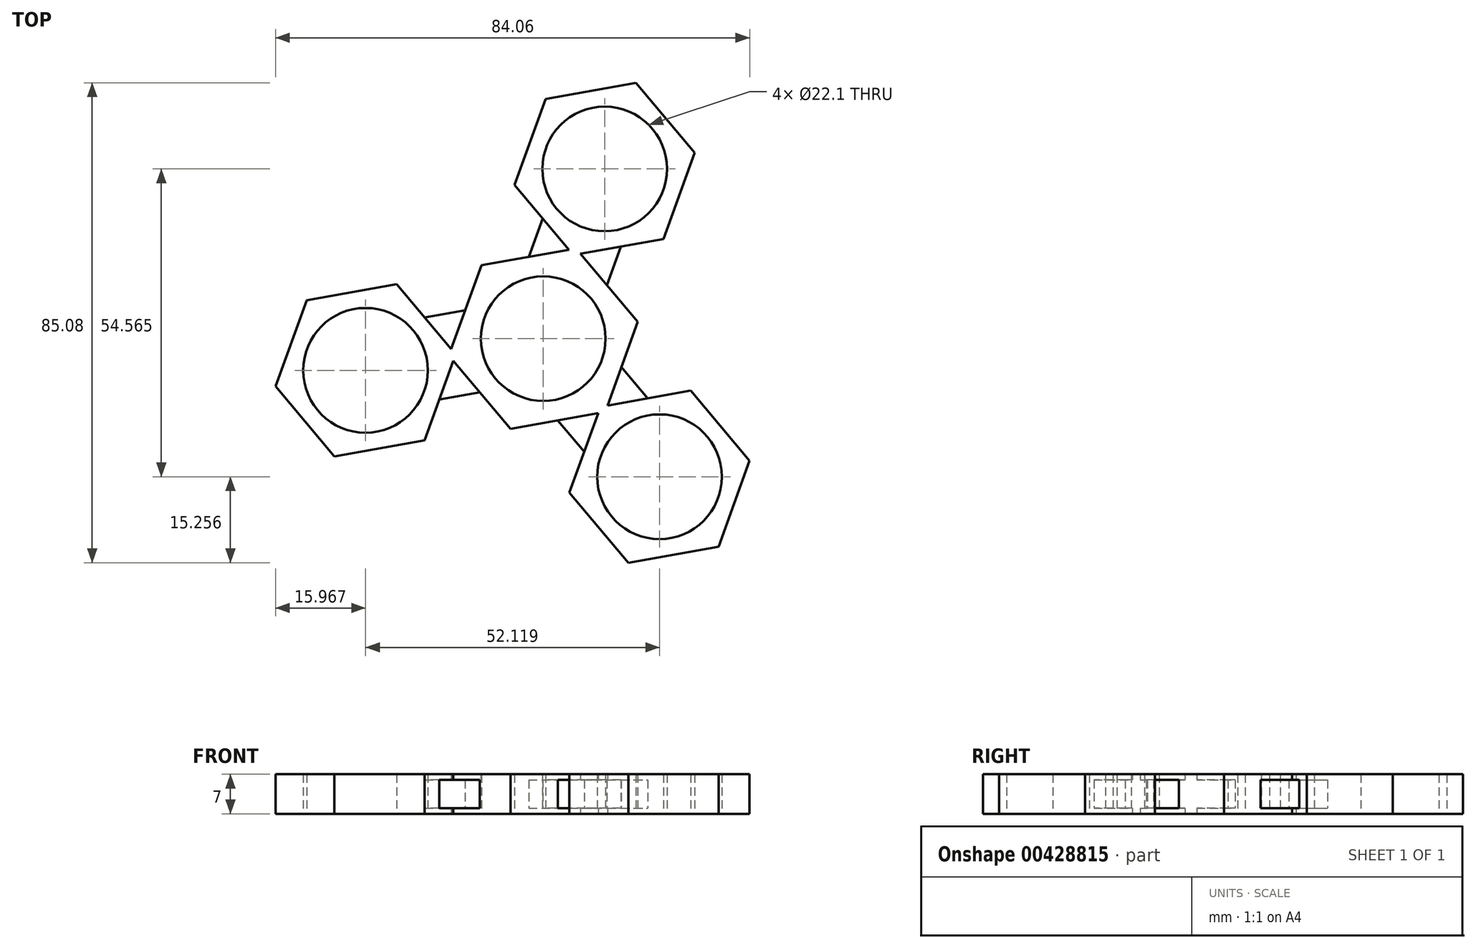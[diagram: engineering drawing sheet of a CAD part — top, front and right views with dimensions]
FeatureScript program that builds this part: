
annotation { "Feature Type Name" : "Feature", "Feature Type Description" : "" }
export const myFeature = defineFeature(function(context is Context, id is Id, definition is map)
    precondition{}
    {
        {
            var Q0;
            Q0=qCreatedBy(makeId("Top.planeOp"),FACE);
            var sketch = newSketch(context, id + "F0", { "sketchPlane" : qUnion([Q0])});
            skCircle(sketch, "E0", {"center": v(0, 0) * mm, "radius": 11.05 * mm});
            skCircle(sketch, "E1.cCircle", {"center": v(0, 0) * mm, "radius": 14.73 * mm, "construction": true});
            skLineSegment(sketch, "E1.0", {"start": v(16.75, 2.99) * mm, "end": v(10.96, -13.01) * mm});
            skLineSegment(sketch, "E1.1", {"start": v(10.96, -13.01) * mm, "end": v(-5.79, -16) * mm});
            skLineSegment(sketch, "E1.2", {"start": v(-5.79, -16) * mm, "end": v(-16.75, -2.99) * mm});
            skLineSegment(sketch, "E1.3", {"start": v(-16.75, -2.99) * mm, "end": v(-10.96, 13.01) * mm});
            skLineSegment(sketch, "E1.4", {"start": v(-10.96, 13.01) * mm, "end": v(5.79, 16) * mm});
            skLineSegment(sketch, "E1.5", {"start": v(5.79, 16) * mm, "end": v(16.75, 2.99) * mm});
            skPoint(sketch, "E1.0.midPoint", {"position": v(13.85, -5.01) * mm});
            skLineSegment(sketch, "E2", {"start": v(0, 0) * mm, "end": v(10.89, 30.1) * mm});
            skCircle(sketch, "E3", {"center": v(10.89, 30.1) * mm, "radius": 11.05 * mm});
            skCircle(sketch, "E4.0", {"center": v(10.89, 30.1) * mm, "radius": 14.05 * mm});
            skCircle(sketch, "E5.cCircle", {"center": v(10.89, 30.1) * mm, "radius": 14.05 * mm, "construction": true});
            skLineSegment(sketch, "E5.0", {"start": v(-5.08, 27.24) * mm, "end": v(0.44, 42.5) * mm});
            skLineSegment(sketch, "E5.1", {"start": v(0.44, 42.5) * mm, "end": v(16.4, 45.35) * mm});
            skLineSegment(sketch, "E5.2", {"start": v(16.4, 45.35) * mm, "end": v(26.86, 32.94) * mm});
            skLineSegment(sketch, "E5.3", {"start": v(26.86, 32.94) * mm, "end": v(21.34, 17.68) * mm});
            skLineSegment(sketch, "E5.4", {"start": v(21.34, 17.68) * mm, "end": v(5.37, 14.84) * mm});
            skLineSegment(sketch, "E5.5", {"start": v(5.37, 14.84) * mm, "end": v(-5.08, 27.24) * mm});
            skPoint(sketch, "E5.0.midPoint", {"position": v(-2.32, 34.87) * mm});
            skLineSegment(sketch, "E6", {"start": v(-2.59, 14.5) * mm, "end": v(0, 21.65) * mm});
            skLineSegment(sketch, "E7.MirrorCS", {"start": v(11.27, 9.5) * mm, "end": v(13.85, 16.64) * mm});
            skCircle(sketch, "E8.1.0", {"center": v(-31.5, -5.62) * mm, "radius": 14.05 * mm, "construction": true});
            skLineSegment(sketch, "E8.1.1", {"start": v(-11.27, -9.5) * mm, "end": v(-18.75, -10.83) * mm});
            skLineSegment(sketch, "E8.1.2", {"start": v(-15.53, -2.77) * mm, "end": v(-21.05, -18.02) * mm});
            skLineSegment(sketch, "E8.1.3", {"start": v(-25.98, 9.64) * mm, "end": v(-15.53, -2.77) * mm});
            skLineSegment(sketch, "E8.1.4", {"start": v(-13.85, 5.01) * mm, "end": v(-21.34, 3.68) * mm});
            skLineSegment(sketch, "E8.1.5", {"start": v(-41.96, 6.8) * mm, "end": v(-25.98, 9.64) * mm});
            skLineSegment(sketch, "E8.1.6", {"start": v(-47.47, -8.46) * mm, "end": v(-41.96, 6.8) * mm});
            skLineSegment(sketch, "E8.1.7", {"start": v(-37.02, -20.87) * mm, "end": v(-47.47, -8.46) * mm});
            skLineSegment(sketch, "E8.1.8", {"start": v(-21.05, -18.02) * mm, "end": v(-37.02, -20.87) * mm});
            skCircle(sketch, "E8.1.9", {"center": v(-31.5, -5.62) * mm, "radius": 11.05 * mm});
            skCircle(sketch, "E8.2.0", {"center": v(20.62, -24.47) * mm, "radius": 14.05 * mm, "construction": true});
            skLineSegment(sketch, "E8.2.1", {"start": v(13.85, -5.01) * mm, "end": v(18.75, -10.83) * mm});
            skLineSegment(sketch, "E8.2.2", {"start": v(10.16, -12.07) * mm, "end": v(26.14, -9.22) * mm});
            skLineSegment(sketch, "E8.2.3", {"start": v(4.64, -27.32) * mm, "end": v(10.16, -12.07) * mm});
            skLineSegment(sketch, "E8.2.4", {"start": v(2.59, -14.5) * mm, "end": v(7.48, -20.32) * mm});
            skLineSegment(sketch, "E8.2.5", {"start": v(15.1, -39.73) * mm, "end": v(4.64, -27.32) * mm});
            skLineSegment(sketch, "E8.2.6", {"start": v(31.07, -36.88) * mm, "end": v(15.1, -39.73) * mm});
            skLineSegment(sketch, "E8.2.7", {"start": v(36.59, -21.63) * mm, "end": v(31.07, -36.88) * mm});
            skLineSegment(sketch, "E8.2.8", {"start": v(26.14, -9.22) * mm, "end": v(36.59, -21.63) * mm});
            skCircle(sketch, "E8.2.9", {"center": v(20.62, -24.47) * mm, "radius": 11.05 * mm});
            skSolve(sketch);
        }
        {
            var Q0;
            {var subQ0=sQuery(id+"F0.wireOp",EDGE,"E5.1");var subQ1=sQuery(id+"F0.wireOp",EDGE,"E4.0");var subQ2=makeQuery(id+"F0.imprint","INTERSECT",VERTEX,{"derivedFrom":[subQ1,subQ0]});Q0=makeQuery(id+"F0.imprint","IMPRINT",FACE,{"disambiguationData":[TD([[makeQuery(id+"F0.imprint","IMPRINT",EDGE,{"disambiguationData":[TD([[subQ2,1.0]])],"derivedFrom":subQ1}),-1.0]])]});}
            var Q1;
            {var subQ0=sQuery(id+"F0.wireOp",EDGE,"E5.1");var subQ1=sQuery(id+"F0.wireOp",EDGE,"E4.0");var subQ2=makeQuery(id+"F0.imprint","INTERSECT",VERTEX,{"derivedFrom":[subQ1,subQ0]});Q1=makeQuery(id+"F0.imprint","IMPRINT",FACE,{"disambiguationData":[TD([[makeQuery(id+"F0.imprint","IMPRINT",EDGE,{"disambiguationData":[TD([[subQ2,-1.0]])],"derivedFrom":subQ1}),-1.0]])]});}
            var Q2;
            {var subQ0=sQuery(id+"F0.wireOp",EDGE,"E5.2");var subQ1=sQuery(id+"F0.wireOp",EDGE,"E4.0");var subQ2=makeQuery(id+"F0.imprint","INTERSECT",VERTEX,{"derivedFrom":[subQ1,subQ0]});Q2=makeQuery(id+"F0.imprint","IMPRINT",FACE,{"disambiguationData":[TD([[makeQuery(id+"F0.imprint","IMPRINT",EDGE,{"disambiguationData":[TD([[subQ2,1.0]])],"derivedFrom":subQ1}),-1.0]])]});}
            var Q3;
            {var subQ0=sQuery(id+"F0.wireOp",EDGE,"E5.0");var subQ1=sQuery(id+"F0.wireOp",EDGE,"E4.0");var subQ2=makeQuery(id+"F0.imprint","INTERSECT",VERTEX,{"derivedFrom":[subQ1,subQ0]});Q3=makeQuery(id+"F0.imprint","IMPRINT",FACE,{"disambiguationData":[TD([[makeQuery(id+"F0.imprint","IMPRINT",EDGE,{"disambiguationData":[TD([[subQ2,-1.0]])],"derivedFrom":subQ1}),-1.0]])]});}
            var Q4;
            {var subQ0=sQuery(id+"F0.wireOp",EDGE,"E7.MirrorCS");var subQ1=sQuery(id+"F0.wireOp",EDGE,"E4.0");var subQ2=makeQuery(id+"F0.imprint","INTERSECT",VERTEX,{"derivedFrom":[subQ1,subQ0]});Q4=makeQuery(id+"F0.imprint","IMPRINT",FACE,{"disambiguationData":[TD([[makeQuery(id+"F0.imprint","IMPRINT",EDGE,{"disambiguationData":[TD([[subQ2,-1.0]])],"derivedFrom":subQ1}),-1.0]])]});}
            var Q5;
            {var subQ0=sQuery(id+"F0.wireOp",EDGE,"E6");var subQ1=sQuery(id+"F0.wireOp",EDGE,"E4.0");var subQ2=makeQuery(id+"F0.imprint","INTERSECT",VERTEX,{"derivedFrom":[subQ1,subQ0]});Q5=makeQuery(id+"F0.imprint","IMPRINT",FACE,{"disambiguationData":[TD([[makeQuery(id+"F0.imprint","IMPRINT",EDGE,{"disambiguationData":[TD([[subQ2,-1.0]])],"derivedFrom":subQ1}),-1.0]])]});}
            var Q6;
            {var subQ0=sQuery(id+"F0.wireOp",EDGE,"E7.MirrorCS");var subQ1=sQuery(id+"F0.wireOp",EDGE,"E4.0");var subQ2=makeQuery(id+"F0.imprint","INTERSECT",VERTEX,{"derivedFrom":[subQ1,subQ0]});Q6=makeQuery(id+"F0.imprint","IMPRINT",FACE,{"disambiguationData":[TD([[makeQuery(id+"F0.imprint","IMPRINT",EDGE,{"disambiguationData":[TD([[subQ2,1.0]])],"derivedFrom":subQ1}),-1.0]])]});}
            var Q7;
            {var subQ6=sQuery(id+"F0.wireOp",EDGE,"E8.2.5");Q7=makeQuery(id+"F0.imprint","IMPRINT",FACE,{"disambiguationData":[TD([[makeQuery(id+"F0.imprint","IMPRINT",EDGE,{"derivedFrom":subQ6}),-1.0]])]});}
            var Q8;
            {var subQ1=sQuery(id+"F0.wireOp",EDGE,"E8.1.5");Q8=makeQuery(id+"F0.imprint","IMPRINT",FACE,{"disambiguationData":[TD([[makeQuery(id+"F0.imprint","IMPRINT",EDGE,{"derivedFrom":subQ1}),-1.0]])]});}
            var Q9;
            Q9=makeQuery(id+"F0.imprint","IMPRINT",FACE,{"disambiguationData":[TD([[makeQuery(id+"F0.imprint","IMPRINT",EDGE,{"derivedFrom":sQuery(id+"F0.wireOp",EDGE,"E3")}),-1.0]])]});
            var Q10;
            Q10=makeQuery(id+"F0.imprint","IMPRINT",FACE,{"disambiguationData":[TD([[makeQuery(id+"F0.imprint","IMPRINT",EDGE,{"derivedFrom":sQuery(id+"F0.wireOp",EDGE,"E0")}),-1.0]])]});
            var Q11;
            {var subQ0=sQuery(id+"F0.wireOp",EDGE,"E2");var subQ5=sQuery(id+"F0.wireOp",EDGE,"E4.0");var subQ7=makeQuery(id+"F0.imprint","INTERSECT",VERTEX,{"derivedFrom":[subQ0,subQ5]});Q11=makeQuery(id+"F0.imprint","IMPRINT",FACE,{"disambiguationData":[TD([[makeQuery(id+"F0.imprint","IMPRINT",EDGE,{"disambiguationData":[TD([[subQ7,-1.0]])],"derivedFrom":subQ5}),-1.0]])]});}
            var Q12;
            {var subQ0=sQuery(id+"F0.wireOp",EDGE,"E2");var subQ5=sQuery(id+"F0.wireOp",EDGE,"E4.0");var subQ6=makeQuery(id+"F0.imprint","INTERSECT",VERTEX,{"derivedFrom":[subQ0,subQ5]});Q12=makeQuery(id+"F0.imprint","IMPRINT",FACE,{"disambiguationData":[TD([[makeQuery(id+"F0.imprint","IMPRINT",EDGE,{"disambiguationData":[TD([[subQ6,1.0]])],"derivedFrom":subQ5}),-1.0]])]});}
            var Q13;
            {var subQ1=sQuery(id+"F0.wireOp",EDGE,"E1.4");var subQ3=sQuery(id+"F0.wireOp",EDGE,"E5.5");var subQ4=makeQuery(id+"F0.imprint","INTERSECT",VERTEX,{"derivedFrom":[subQ1,subQ3]});Q13=makeQuery(id+"F0.imprint","IMPRINT",FACE,{"disambiguationData":[TD([[makeQuery(id+"F0.imprint","IMPRINT",EDGE,{"disambiguationData":[TD([[subQ4,-1.0]])],"derivedFrom":subQ1}),-1.0]])]});}
            var Q14;
            {var subQ1=sQuery(id+"F0.wireOp",EDGE,"E1.5");var subQ3=sQuery(id+"F0.wireOp",EDGE,"E5.4");var subQ4=makeQuery(id+"F0.imprint","INTERSECT",VERTEX,{"derivedFrom":[subQ1,subQ3]});Q14=makeQuery(id+"F0.imprint","IMPRINT",FACE,{"disambiguationData":[TD([[makeQuery(id+"F0.imprint","IMPRINT",EDGE,{"disambiguationData":[TD([[subQ4,1.0]])],"derivedFrom":subQ1}),-1.0]])]});}
            var Q15;
            {var subQ0=sQuery(id+"F0.wireOp",EDGE,"E1.1");var subQ1=sQuery(id+"F0.wireOp",EDGE,"E1.0");var subQ2=makeQuery(id+"F0.imprint","INTERSECT",VERTEX,{"derivedFrom":[subQ1,subQ0]});Q15=makeQuery(id+"F0.imprint","IMPRINT",FACE,{"disambiguationData":[TD([[makeQuery(id+"F0.imprint","IMPRINT",EDGE,{"disambiguationData":[TD([[subQ2,1.0]])],"derivedFrom":subQ1}),-1.0]])]});}
            var Q16;
            {var subQ0=sQuery(id+"F0.wireOp",EDGE,"E1.3");var subQ1=sQuery(id+"F0.wireOp",EDGE,"E1.2");var subQ2=makeQuery(id+"F0.imprint","INTERSECT",VERTEX,{"derivedFrom":[subQ1,subQ0]});Q16=makeQuery(id+"F0.imprint","IMPRINT",FACE,{"disambiguationData":[TD([[makeQuery(id+"F0.imprint","IMPRINT",EDGE,{"disambiguationData":[TD([[subQ2,1.0]])],"derivedFrom":subQ1}),-1.0]])]});}
            extrude(context, id + "F1", {"entities" : qUnion([Q0, Q1, Q2, Q3, Q4, Q5, Q6, Q7, Q8, Q9, Q10, Q11, Q12, Q13, Q14, Q15, Q16]), "endBound" : BoundingType.SYMMETRIC, "depth" : 7 * mm});
        }
        {
            var Q0;
            {var subQ0=sQuery(id+"F0.wireOp",EDGE,"E6");var subQ1=sQuery(id+"F0.wireOp",EDGE,"E1.4");var subQ2=makeQuery(id+"F0.imprint","INTERSECT",VERTEX,{"derivedFrom":[subQ1,subQ0]});Q0=makeQuery(id+"F0.imprint","IMPRINT",FACE,{"disambiguationData":[TD([[makeQuery(id+"F0.imprint","IMPRINT",EDGE,{"disambiguationData":[TD([[subQ2,-1.0]])],"derivedFrom":subQ1}),1.0]])]});}
            var Q1;
            {var subQ0=sQuery(id+"F0.wireOp",EDGE,"E7.MirrorCS");var subQ1=sQuery(id+"F0.wireOp",EDGE,"E1.5");var subQ2=makeQuery(id+"F0.imprint","INTERSECT",VERTEX,{"derivedFrom":[subQ1,subQ0]});Q1=makeQuery(id+"F0.imprint","IMPRINT",FACE,{"disambiguationData":[TD([[makeQuery(id+"F0.imprint","IMPRINT",EDGE,{"disambiguationData":[TD([[subQ2,1.0]])],"derivedFrom":subQ1}),1.0]])]});}
            var Q2;
            {var subQ0=sQuery(id+"F0.wireOp",EDGE,"E8.2.1");var subQ1=sQuery(id+"F0.wireOp",EDGE,"E1.0");var subQ2=makeQuery(id+"F0.imprint","INTERSECT",VERTEX,{"derivedFrom":[subQ1,subQ0]});Q2=makeQuery(id+"F0.imprint","IMPRINT",FACE,{"disambiguationData":[TD([[makeQuery(id+"F0.imprint","IMPRINT",EDGE,{"disambiguationData":[TD([[subQ2,-1.0]])],"derivedFrom":subQ1}),1.0]])]});}
            var Q3;
            {var subQ0=sQuery(id+"F0.wireOp",EDGE,"E8.2.4");var subQ1=sQuery(id+"F0.wireOp",EDGE,"E1.1");var subQ2=makeQuery(id+"F0.imprint","INTERSECT",VERTEX,{"derivedFrom":[subQ1,subQ0]});Q3=makeQuery(id+"F0.imprint","IMPRINT",FACE,{"disambiguationData":[TD([[makeQuery(id+"F0.imprint","IMPRINT",EDGE,{"disambiguationData":[TD([[subQ2,1.0]])],"derivedFrom":subQ1}),1.0]])]});}
            var Q4;
            {var subQ0=sQuery(id+"F0.wireOp",EDGE,"E8.1.1");var subQ1=sQuery(id+"F0.wireOp",EDGE,"E1.2");var subQ2=makeQuery(id+"F0.imprint","INTERSECT",VERTEX,{"derivedFrom":[subQ1,subQ0]});Q4=makeQuery(id+"F0.imprint","IMPRINT",FACE,{"disambiguationData":[TD([[makeQuery(id+"F0.imprint","IMPRINT",EDGE,{"disambiguationData":[TD([[subQ2,-1.0]])],"derivedFrom":subQ1}),1.0]])]});}
            var Q5;
            {var subQ0=sQuery(id+"F0.wireOp",EDGE,"E8.1.4");var subQ1=sQuery(id+"F0.wireOp",EDGE,"E1.3");var subQ2=makeQuery(id+"F0.imprint","INTERSECT",VERTEX,{"derivedFrom":[subQ1,subQ0]});Q5=makeQuery(id+"F0.imprint","IMPRINT",FACE,{"disambiguationData":[TD([[makeQuery(id+"F0.imprint","IMPRINT",EDGE,{"disambiguationData":[TD([[subQ2,1.0]])],"derivedFrom":subQ1}),1.0]])]});}
            extrude(context, id + "F2", {"entities" : qUnion([Q0, Q1, Q2, Q3, Q4, Q5]), "operationType" : NewBodyOperationType.ADD, "endBound" : BoundingType.SYMMETRIC, "depth" : 5 * mm});
        }
    });
